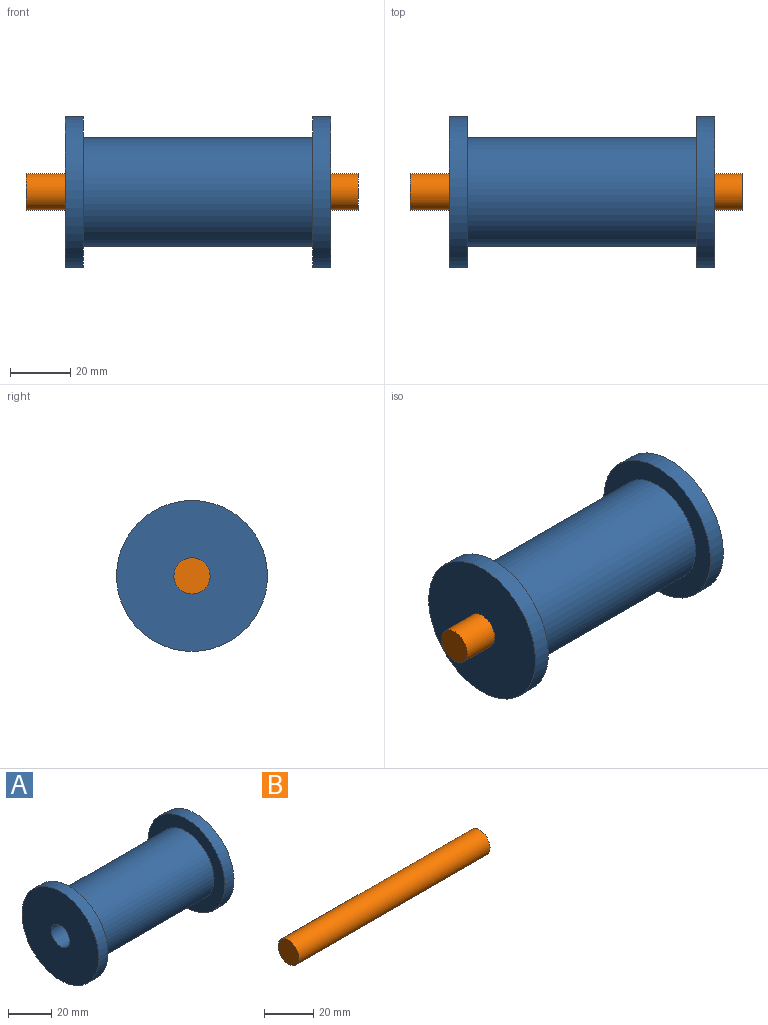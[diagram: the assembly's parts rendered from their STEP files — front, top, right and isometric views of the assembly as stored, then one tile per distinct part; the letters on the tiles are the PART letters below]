
ASSEMBLY  parts=2 mates=1
PART A: 8 faces, bbox 88x50x50 mm
  f0: plane 50x50mm, normal (1,0,0), area 1850.4mm2, adj f1,f7
  f1: cylinder r=25mm len=50mm, axis (1,0,0), area 942.5mm2, adj f0,f2
  f2: plane 50x50mm, normal (-1,0,0), area 945.6mm2, adj f1,f3
  f3: cylinder r=18mm len=76mm, axis (1,0,0), area 8595.4mm2, adj f2,f4
  f4: plane 50x50mm, normal (1,0,0), area 945.6mm2, adj f3,f5
  f5: cylinder r=25mm len=50mm, axis (1,0,0), area 942.5mm2, adj f4,f6
  f6: plane 50x50mm, normal (-1,0,0), area 1850.4mm2, adj f5,f7
  f7: cylinder r=6mm len=88mm, axis (1,0,0), area 3317.5mm2, adj f0,f6
PART B: 3 faces, bbox 110x12x12 mm
  f0: plane 12x12mm, normal (1,0,0), area 113.1mm2, adj f1
  f1: cylinder r=6mm len=110mm, axis (1,0,0), area 4146.9mm2, adj f0,f2
  f2: plane 12x12mm, normal (-1,0,0), area 113.1mm2, adj f1
PLACE A t=(2.06,3.12,2.9)mm
PLACE B t=(0.06,3.12,2.9)mm
MATE revolute B.f1 <-> A.f1  axis (1,0,0) through (0.06,3.12,2.9)mm
